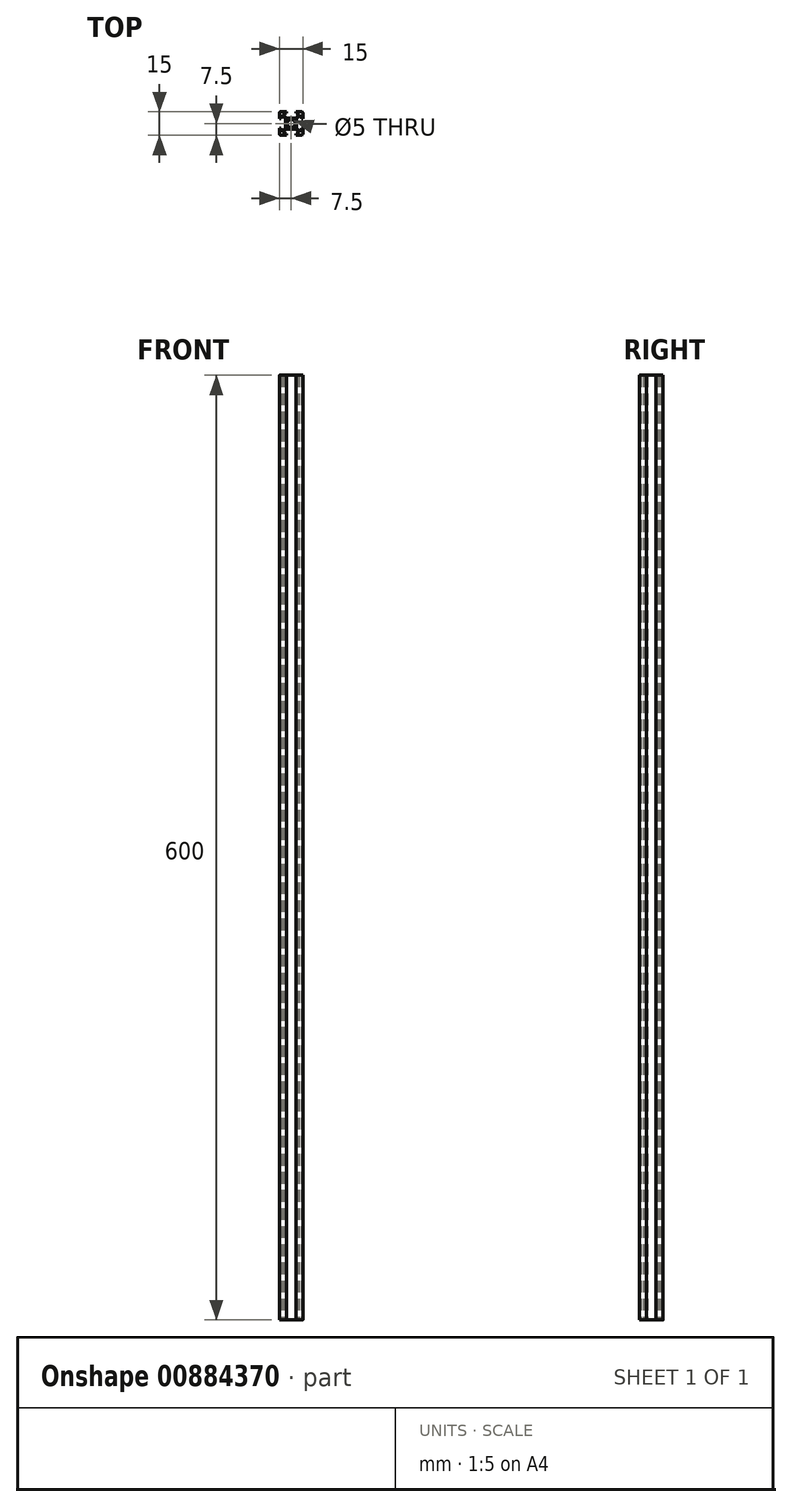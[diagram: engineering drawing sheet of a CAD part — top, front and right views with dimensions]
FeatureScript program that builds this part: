
annotation { "Feature Type Name" : "Feature", "Feature Type Description" : "" }
export const myFeature = defineFeature(function(context is Context, id is Id, definition is map)
    precondition{}
    {
        {
            var Q0;
            Q0=qCreatedBy(makeId("Top.planeOp"),FACE);
            var sketch = newSketch(context, id + "F0", { "sketchPlane" : qUnion([Q0])});
            skCircle(sketch, "E0", {"center": v(0, 0) * mm, "radius": 2.5 * mm});
            skLineSegment(sketch, "E1.bottom", {"start": v(6.5, 7.5) * mm, "end": v(3, 7.5) * mm});
            skLineSegment(sketch, "E1.top", {"start": v(6.5, -7.5) * mm, "end": v(3, -7.5) * mm});
            skLineSegment(sketch, "E1.left", {"start": v(7.5, 6.5) * mm, "end": v(7.5, 3) * mm});
            skLineSegment(sketch, "E1.right", {"start": v(-7.5, 6.5) * mm, "end": v(-7.5, 3) * mm});
            skPoint(sketch, "E2.visualSharp", {"position": v(-7.5, 7.5) * mm});
            skArc(sketch, "E2.filletArc", {"start": v(-6.5, 7.5) * mm, "mid": v(-7.2, 7.2) * mm, "end": v(-7.5, 6.5) * mm});
            skPoint(sketch, "E3.visualSharp", {"position": v(7.5, 7.5) * mm});
            skArc(sketch, "E3.filletArc", {"start": v(7.5, 6.5) * mm, "mid": v(7.2, 7.2) * mm, "end": v(6.5, 7.5) * mm});
            skPoint(sketch, "E4.visualSharp", {"position": v(7.5, -7.5) * mm});
            skArc(sketch, "E4.filletArc", {"start": v(6.5, -7.5) * mm, "mid": v(7.2, -7.2) * mm, "end": v(7.5, -6.5) * mm});
            skPoint(sketch, "E5.visualSharp", {"position": v(-7.5, -7.5) * mm});
            skArc(sketch, "E5.filletArc", {"start": v(-7.5, -6.5) * mm, "mid": v(-7.2, -7.2) * mm, "end": v(-6.5, -7.5) * mm});
            skLineSegment(sketch, "E6", {"start": v(-3, 7.5) * mm, "end": v(-3, 6.5) * mm});
            skLineSegment(sketch, "E7", {"start": v(3, 7.5) * mm, "end": v(3, 6.5) * mm});
            skLineSegment(sketch, "E8", {"start": v(-4.5, 6.5) * mm, "end": v(-4.5, 5) * mm});
            skLineSegment(sketch, "E9", {"start": v(4.5, 5) * mm, "end": v(4.5, 6.5) * mm});
            skLineSegment(sketch, "E10", {"start": v(4.5, 6.5) * mm, "end": v(3, 6.5) * mm});
            skLineSegment(sketch, "E11", {"start": v(-3, 3.5) * mm, "end": v(3, 3.5) * mm});
            skLineSegment(sketch, "E12", {"start": v(3, 3.5) * mm, "end": v(4.5, 5) * mm});
            skLineSegment(sketch, "E13", {"start": v(-3, 3.5) * mm, "end": v(-4.5, 5) * mm});
            skLineSegment(sketch, "E14.trimOffspring", {"start": v(-3, 6.5) * mm, "end": v(-4.5, 6.5) * mm});
            skLineSegment(sketch, "E15", {"start": v(-3, -7.5) * mm, "end": v(-3, -6.5) * mm});
            skLineSegment(sketch, "E16", {"start": v(-3, -6.5) * mm, "end": v(-4.5, -6.5) * mm});
            skLineSegment(sketch, "E17", {"start": v(-4.5, -6.5) * mm, "end": v(-4.5, -5) * mm});
            skLineSegment(sketch, "E18", {"start": v(-4.5, -5) * mm, "end": v(-3, -3.5) * mm});
            skLineSegment(sketch, "E19", {"start": v(-3, -3.5) * mm, "end": v(3, -3.5) * mm});
            skLineSegment(sketch, "E20", {"start": v(3, -3.5) * mm, "end": v(4.5, -5) * mm});
            skLineSegment(sketch, "E21", {"start": v(4.5, -5) * mm, "end": v(4.5, -6.5) * mm});
            skLineSegment(sketch, "E22", {"start": v(4.5, -6.5) * mm, "end": v(3, -6.5) * mm});
            skLineSegment(sketch, "E23", {"start": v(3, -6.5) * mm, "end": v(3, -7.5) * mm});
            skPoint(sketch, "E24", {"position": v(0, 7.5) * mm});
            skPoint(sketch, "E25", {"position": v(0, -7.5) * mm});
            skPoint(sketch, "E26", {"position": v(7.5, 0) * mm});
            skPoint(sketch, "E27", {"position": v(-7.5, 0) * mm});
            skLineSegment(sketch, "E28", {"start": v(7.5, 3) * mm, "end": v(6.5, 3) * mm});
            skLineSegment(sketch, "E29", {"start": v(6.5, 3) * mm, "end": v(6.5, 4.5) * mm});
            skLineSegment(sketch, "E30", {"start": v(6.5, 4.5) * mm, "end": v(5, 4.5) * mm});
            skLineSegment(sketch, "E31", {"start": v(5, 4.5) * mm, "end": v(3.5, 3) * mm});
            skLineSegment(sketch, "E32", {"start": v(3.5, 3) * mm, "end": v(3.5, -3) * mm});
            skLineSegment(sketch, "E33", {"start": v(3.5, -3) * mm, "end": v(5, -4.5) * mm});
            skLineSegment(sketch, "E34", {"start": v(5, -4.5) * mm, "end": v(6.5, -4.5) * mm});
            skLineSegment(sketch, "E35", {"start": v(6.5, -4.5) * mm, "end": v(6.5, -3) * mm});
            skLineSegment(sketch, "E36", {"start": v(6.5, -3) * mm, "end": v(7.5, -3) * mm});
            skLineSegment(sketch, "E37.trimOffspring", {"start": v(-3, 7.5) * mm, "end": v(-6.5, 7.5) * mm});
            skLineSegment(sketch, "E38.trimOffspring", {"start": v(7.5, -3) * mm, "end": v(7.5, -6.5) * mm});
            skLineSegment(sketch, "E39.trimOffspring", {"start": v(-3, -7.5) * mm, "end": v(-6.5, -7.5) * mm});
            skLineSegment(sketch, "E40", {"start": v(-7.5, 3) * mm, "end": v(-6.5, 3) * mm});
            skLineSegment(sketch, "E41", {"start": v(-6.5, 3) * mm, "end": v(-6.5, 4.5) * mm});
            skLineSegment(sketch, "E42", {"start": v(-6.5, 4.5) * mm, "end": v(-5, 4.5) * mm});
            skLineSegment(sketch, "E43", {"start": v(-5, 4.5) * mm, "end": v(-3.5, 3) * mm});
            skLineSegment(sketch, "E44", {"start": v(-3.5, 3) * mm, "end": v(-3.5, -3) * mm});
            skLineSegment(sketch, "E45", {"start": v(-3.5, -3) * mm, "end": v(-5, -4.5) * mm});
            skLineSegment(sketch, "E46", {"start": v(-5, -4.5) * mm, "end": v(-6.5, -4.5) * mm});
            skLineSegment(sketch, "E47", {"start": v(-6.5, -4.5) * mm, "end": v(-6.5, -3) * mm});
            skLineSegment(sketch, "E48", {"start": v(-6.5, -3) * mm, "end": v(-7.5, -3) * mm});
            skLineSegment(sketch, "E49.trimOffspring", {"start": v(-7.5, -3) * mm, "end": v(-7.5, -6.5) * mm});
            skSolve(sketch);
        }
        {
            var Q0;
            Q0 = qSketchRegion(id + "F0", true);
            extrude(context, id + "F1", {"entities" : qUnion([Q0]), "depth" : 600 * mm, "offsetDistance" : 25 * mm});
        }
    });
